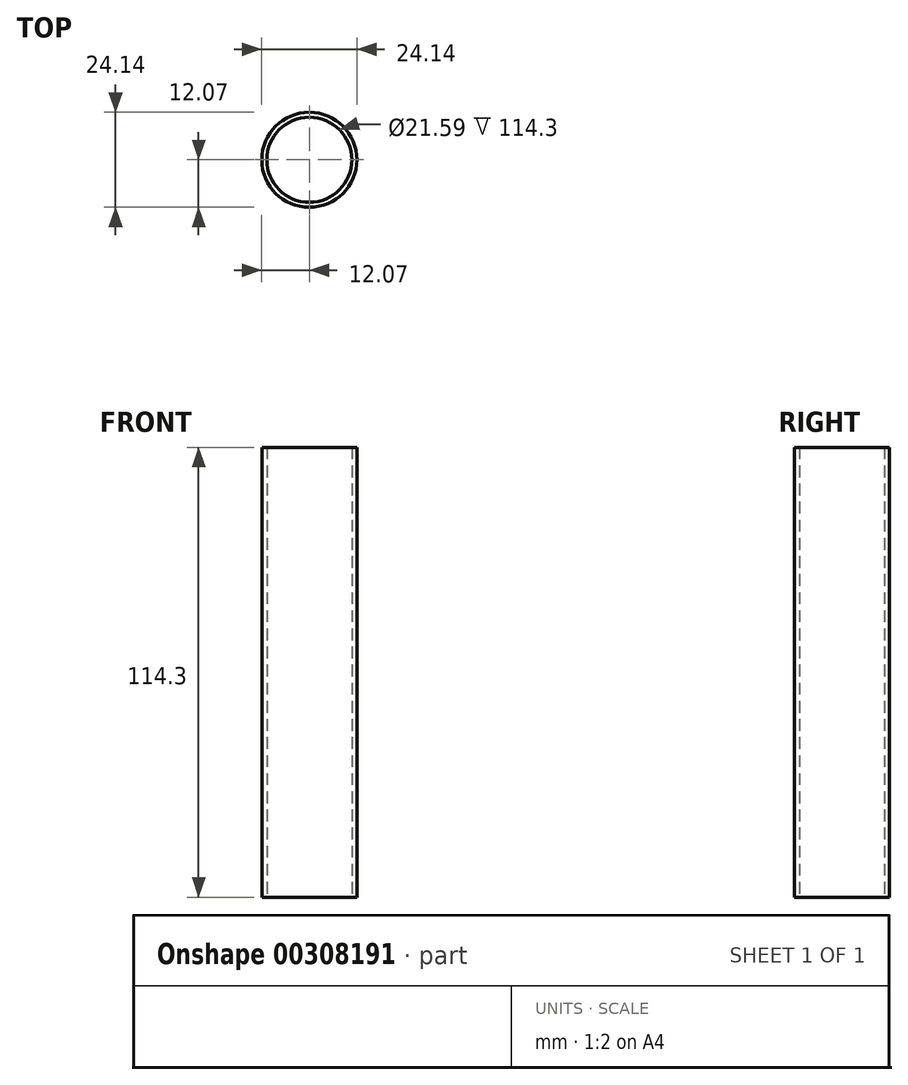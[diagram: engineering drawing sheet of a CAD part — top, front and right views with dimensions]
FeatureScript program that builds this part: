
annotation { "Feature Type Name" : "Feature", "Feature Type Description" : "" }
export const myFeature = defineFeature(function(context is Context, id is Id, definition is map)
    precondition{}
    {
        {
            var Q0;
            Q0=qCreatedBy(makeId("Top.planeOp"),FACE);
            var sketch = newSketch(context, id + "F0", { "sketchPlane" : qUnion([Q0])});
            skCircle(sketch, "E0", {"center": v(0, 0) * mm, "radius": 10.8 * mm});
            skCircle(sketch, "E1", {"center": v(0, 0) * mm, "radius": 12.07 * mm});
            skSolve(sketch);
        }
        {
            var Q0;
            Q0=makeQuery(id+"F0.imprint","IMPRINT",FACE,{"disambiguationData":[TD([[makeQuery(id+"F0.imprint","IMPRINT",EDGE,{"derivedFrom":sQuery(id+"F0.wireOp",EDGE,"E0")}),-1.0]])]});
            extrude(context, id + "F1", {"entities" : qUnion([Q0]), "depth" : 114.3 * mm});
        }
    });
